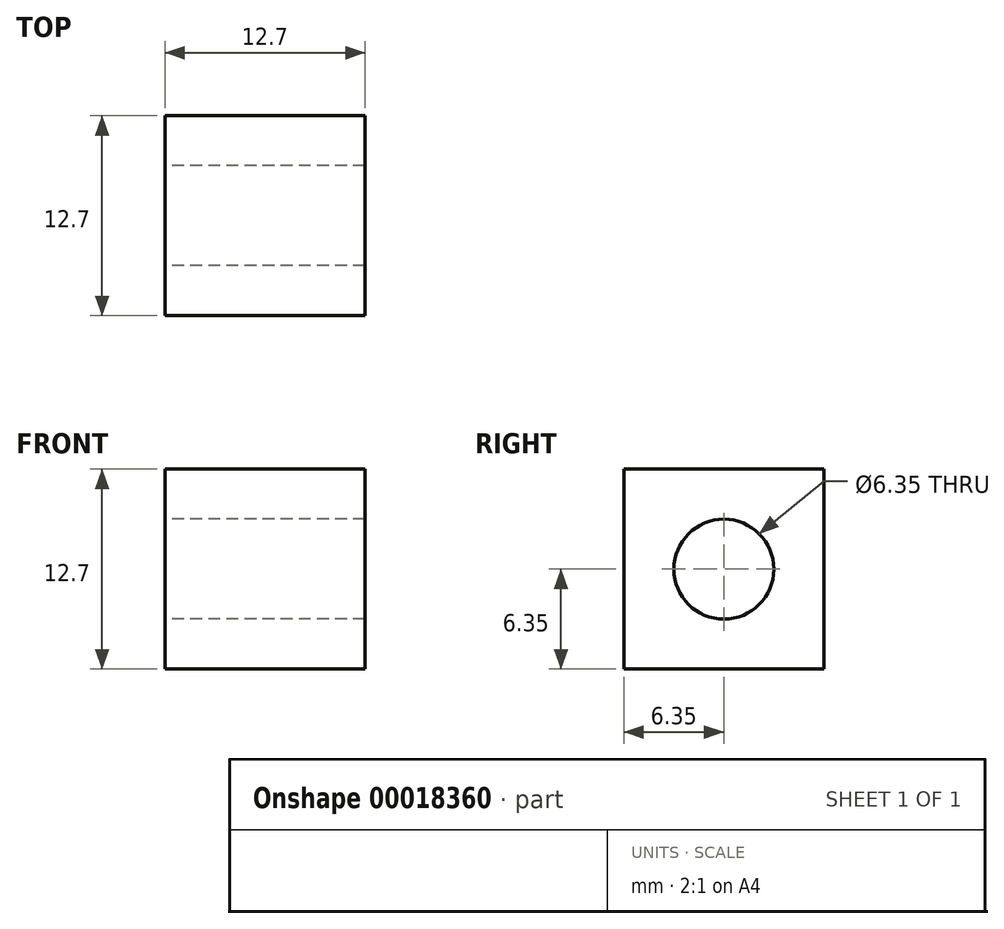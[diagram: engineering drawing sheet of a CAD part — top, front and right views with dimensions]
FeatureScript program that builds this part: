
annotation { "Feature Type Name" : "Feature", "Feature Type Description" : "" }
export const myFeature = defineFeature(function(context is Context, id is Id, definition is map)
    precondition{}
    {
        {
            var Q0;
            Q0=qCreatedBy(makeId("Right.planeOp"),FACE);
            var sketch = newSketch(context, id + "F0", { "sketchPlane" : qUnion([Q0])});
            skLineSegment(sketch, "E0", {"start": v(0, 0) * mm, "end": v(-12.7, 0) * mm});
            skLineSegment(sketch, "E1", {"start": v(-12.7, 0) * mm, "end": v(-12.7, -12.7) * mm});
            skLineSegment(sketch, "E2", {"start": v(0, -12.7) * mm, "end": v(-12.7, -12.7) * mm});
            skLineSegment(sketch, "E3", {"start": v(0, -12.7) * mm, "end": v(0, 0) * mm});
            skCircle(sketch, "E4", {"center": v(-6.35, -6.35) * mm, "radius": 3.18 * mm});
            skSolve(sketch);
        }
        {
            var Q0;
            Q0=makeQuery(id+"F0.imprint","IMPRINT",FACE,{"disambiguationData":[TD([[makeQuery(id+"F0.imprint","IMPRINT",EDGE,{"derivedFrom":sQuery(id+"F0.wireOp",EDGE,"E0")}),1.0]])]});
            extrude(context, id + "F1", {"entities" : qUnion([Q0]), "depth" : 12.7 * mm});
        }
    });
